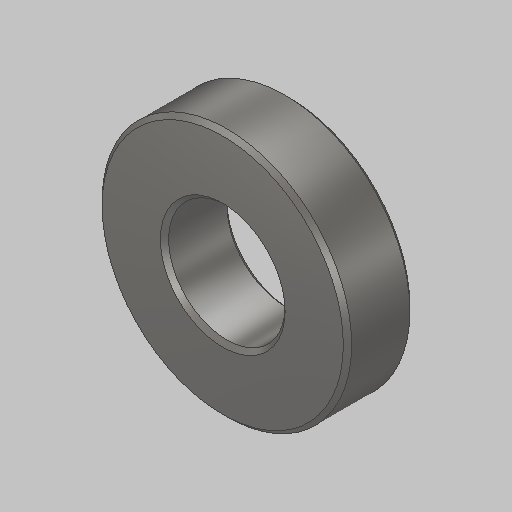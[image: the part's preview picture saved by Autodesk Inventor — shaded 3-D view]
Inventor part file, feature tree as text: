
AUTODESK INVENTOR PART (.ipt)
format: ipt  version: 2023.5 (Build 275446000, 446)  size: 130,560 bytes
history: native  units: in
note: dims shown in document units (in); Inventor stores cm internally (conversion verified against a paired STEP export)
features: extrude x1, chamfer x1
ambient origin geometry x8: Origin, YZ Plane, XZ Plane, XY Plane, X Axis, Y Axis, Z Axis, Center Point
bodies: Solid1 (feature_tree)
feature tree (2):
  extrude  "Extrusion1"  Depth=1.875in
  chamfer  "Chamfer1"  Distance=0.875in
